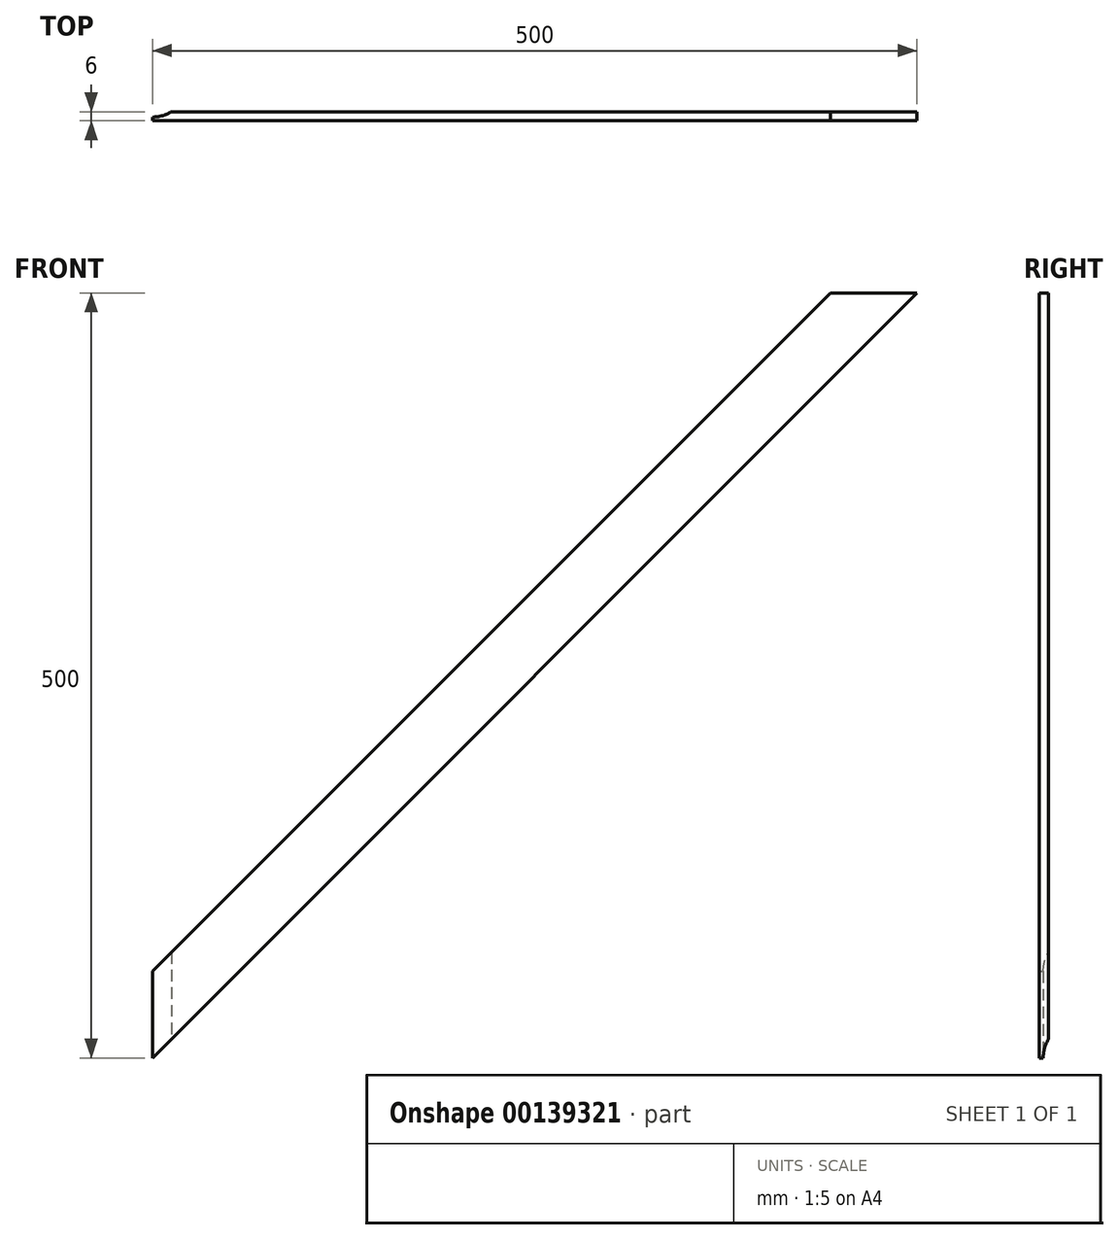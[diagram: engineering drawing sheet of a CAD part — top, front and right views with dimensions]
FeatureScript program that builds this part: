
annotation { "Feature Type Name" : "Feature", "Feature Type Description" : "" }
export const myFeature = defineFeature(function(context is Context, id is Id, definition is map)
    precondition{}
    {
        {
            var Q0;
            Q0=qCreatedBy(makeId("Front.planeOp"),FACE);
            var sketch = newSketch(context, id + "F0", { "sketchPlane" : qUnion([Q0])});
            skLineSegment(sketch, "E0", {"start": v(0, 0) * mm, "end": v(500, 500) * mm});
            skLineSegment(sketch, "E1", {"start": v(0, 0) * mm, "end": v(0, 56.57) * mm});
            skLineSegment(sketch, "E2", {"start": v(500, 500) * mm, "end": v(443.43, 500) * mm});
            skLineSegment(sketch, "E3", {"start": v(0, 56.57) * mm, "end": v(443.43, 500) * mm});
            skPoint(sketch, "E4.end.orphan", {"position": v(50, 0) * mm});
            skSolve(sketch);
        }
        {
            var Q0;
            Q0 = qSketchRegion(id + "F0", true);
            var Q1;
            Q1=makeQuery(id+"F0.imprint","IMPRINT",FACE,{"disambiguationData":[TD([[makeQuery(id+"F0.imprint","IMPRINT",EDGE,{"derivedFrom":sQuery(id+"F0.wireOp",EDGE,"E0")}),1.0]])]});
            extrude(context, id + "F1", {"entities" : qUnion([Q0, Q1]), "depth" : 6 * mm});
        }
        {
            var Q0;
            Q0=qCreatedBy(makeId("Top.planeOp"),FACE);
            var sketch = newSketch(context, id + "F2", { "sketchPlane" : qUnion([Q0])});
            skCircle(sketch, "E5", {"center": v(0, 20.65) * mm, "radius": 24.15 * mm});
            skSolve(sketch);
        }
        {
            var Q0;
            Q0 = qSketchRegion(id + "F2", true);
            extrude(context, id + "F3", {"entities" : qUnion([Q0]), "operationType" : NewBodyOperationType.REMOVE, "endBound" : BoundingType.THROUGH_ALL, "depth" : 25 * mm});
        }
    });
